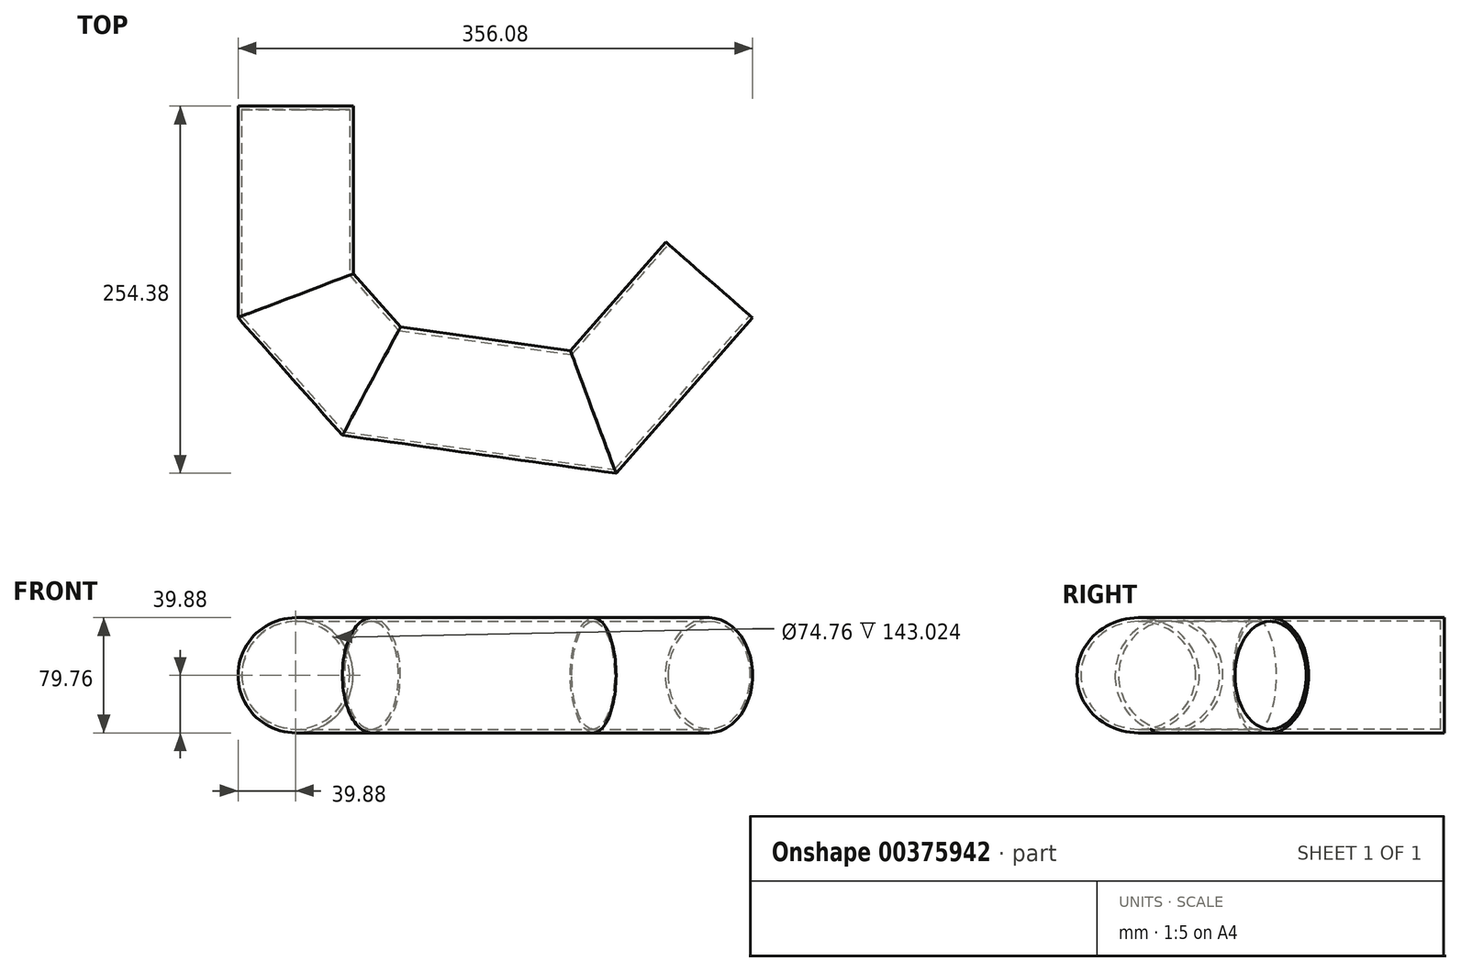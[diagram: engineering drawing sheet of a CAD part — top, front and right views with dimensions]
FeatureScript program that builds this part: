
annotation { "Feature Type Name" : "Feature", "Feature Type Description" : "" }
export const myFeature = defineFeature(function(context is Context, id is Id, definition is map)
    precondition{}
    {
        {
            var Q0;
            Q0=qCreatedBy(makeId("Front.planeOp"),FACE);
            var sketch = newSketch(context, id + "F0", { "sketchPlane" : qUnion([Q0])});
            skCircle(sketch, "E0", {"center": v(0, 0) * mm, "radius": 39.88 * mm});
            skSolve(sketch);
        }
        {
            var Q0;
            Q0=qCreatedBy(makeId("Front.planeOp"),FACE);
            cPlane(context, id + "F1", {"entities" : qUnion([Q0]), "cplaneType" : CPlaneType.OFFSET, "offset" : 102.8 * mm, "width" : 150 * mm, "height" : 150 * mm});
        }
        {
            var Q0;
            Q0=qCreatedBy(makeId("Top.planeOp"),FACE);
            var sketch = newSketch(context, id + "F2", { "sketchPlane" : qUnion([Q0])});
            skLineSegment(sketch, "E1", {"start": v(0, 0) * mm, "end": v(0, -131.3) * mm});
            skLineSegment(sketch, "E2", {"start": v(0, -131.3) * mm, "end": v(52.46, -190.56) * mm});
            skLineSegment(sketch, "E3", {"start": v(52.46, -190.56) * mm, "end": v(205.95, -211.92) * mm});
            skLineSegment(sketch, "E4", {"start": v(205.95, -211.92) * mm, "end": v(286.21, -120.37) * mm});
            skSolve(sketch);
        }
        {
            var Q0;
            Q0=makeQuery(id+"F0.imprint","IMPRINT",FACE,{"disambiguationData":[TD([[makeQuery(id+"F0.imprint","IMPRINT",EDGE,{"derivedFrom":sQuery(id+"F0.wireOp",EDGE,"E0")}),1.0]])]});
            var Q1;
            Q1=qConstructionFilter(qBodyType(qCreatedBy(id+"F2",EDGE),BodyType.WIRE),ConstructionObject.NO);
            sweep(context, id + "F3", {"profiles" : qUnion([Q0]), "path" : qUnion([Q1])});
        }
        {
            var Q0;
            Q0=makeQuery(id+"F3.opSweep","CAP_FACE",FACE,{"disambiguationData":[OSD([sQuery(id+"F0.wireOp",EDGE,"E0"),sQuery(id+"F2.wireOp",VERTEX,"E4.end")])],"isStart":false});
            shell(context, id + "F4", {"entities" : qUnion([Q0]), "thickness" : 2.5 * mm});
        }
    });
